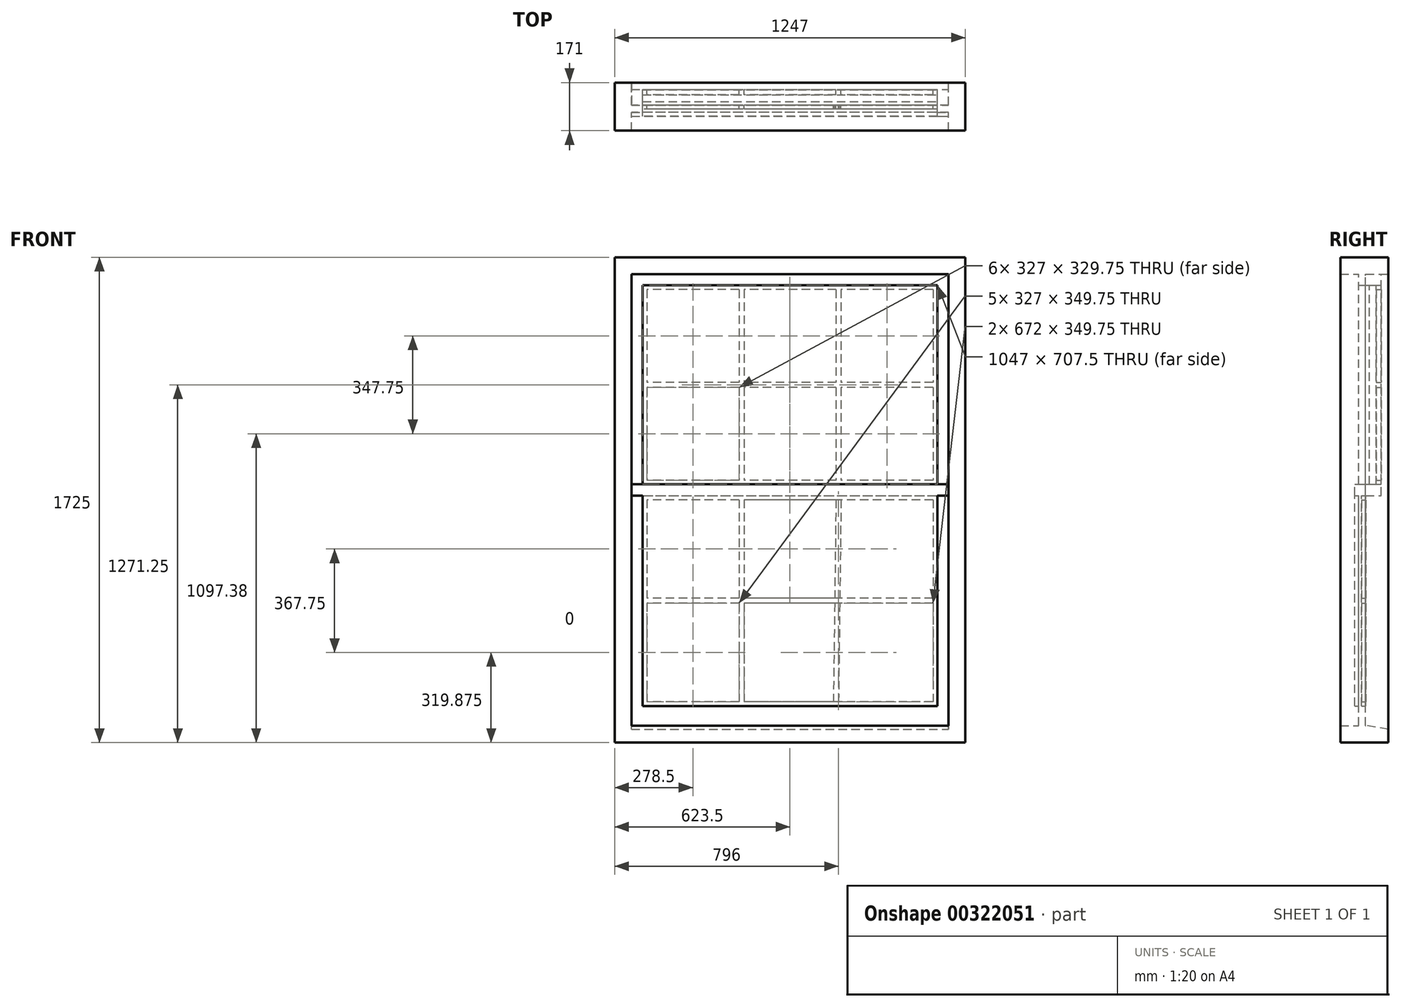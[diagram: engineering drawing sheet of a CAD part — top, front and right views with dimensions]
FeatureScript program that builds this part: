
annotation { "Feature Type Name" : "Feature", "Feature Type Description" : "" }
export const myFeature = defineFeature(function(context is Context, id is Id, definition is map)
    precondition{}
    {
        {
            var Q0;
            Q0=qCreatedBy(makeId("Front.planeOp"),FACE);
            var sketch = newSketch(context, id + "F0", { "sketchPlane" : qUnion([Q0])});
            skLineSegment(sketch, "E0.bottom", {"start": v(0, 0) * mm, "end": v(-1247, 0) * mm});
            skLineSegment(sketch, "E0.top", {"start": v(0, 1725) * mm, "end": v(-1247, 1725) * mm});
            skLineSegment(sketch, "E0.left", {"start": v(0, 0) * mm, "end": v(0, 1725) * mm});
            skLineSegment(sketch, "E0.right", {"start": v(-1247, 0) * mm, "end": v(-1247, 1725) * mm});
            skLineSegment(sketch, "E1.0", {"start": v(-60, 1665) * mm, "end": v(-1187, 1665) * mm});
            skLineSegment(sketch, "E1.1", {"start": v(-60, 60) * mm, "end": v(-60, 1665) * mm});
            skLineSegment(sketch, "E1.2", {"start": v(-60, 60) * mm, "end": v(-1187, 60) * mm});
            skLineSegment(sketch, "E1.3", {"start": v(-1187, 60) * mm, "end": v(-1187, 1665) * mm});
            skLineSegment(sketch, "E2.0", {"start": v(-1147, 130) * mm, "end": v(-1147, 877.5) * mm});
            skLineSegment(sketch, "E2.1", {"start": v(-100, 1625) * mm, "end": v(-1147, 1625) * mm});
            skLineSegment(sketch, "E2.2", {"start": v(-100, 130) * mm, "end": v(-100, 877.5) * mm});
            skLineSegment(sketch, "E3.0", {"start": v(-100, 130) * mm, "end": v(-1147, 130) * mm});
            skLineSegment(sketch, "E4", {"start": v(-1187, 877.5) * mm, "end": v(-60, 877.5) * mm});
            skLineSegment(sketch, "E5.0", {"start": v(-1147, 917.5) * mm, "end": v(-100, 917.5) * mm});
            skPoint(sketch, "E6.orphan", {"position": v(-100, 877.5) * mm});
            skPoint(sketch, "E7.orphan", {"position": v(-1147, 877.5) * mm});
            skLineSegment(sketch, "E8.trimOffspring", {"start": v(-100, 917.5) * mm, "end": v(-100, 1625) * mm});
            skLineSegment(sketch, "E9.trimOffspring", {"start": v(-1147, 917.5) * mm, "end": v(-1147, 1625) * mm});
            skLineSegment(sketch, "E10.bottom", {"start": v(-115, 1610) * mm, "end": v(-442, 1610) * mm});
            skLineSegment(sketch, "E10.top", {"start": v(-115, 1280.25) * mm, "end": v(-442, 1280.25) * mm});
            skLineSegment(sketch, "E10.left", {"start": v(-115, 1610) * mm, "end": v(-115, 1280.25) * mm});
            skLineSegment(sketch, "E10.right", {"start": v(-787, 1610) * mm, "end": v(-787, 1280.25) * mm});
            skLineSegment(sketch, "E11.bottom", {"start": v(-805, 1610) * mm, "end": v(-1132, 1610) * mm});
            skLineSegment(sketch, "E11.top", {"start": v(-805, 1280.25) * mm, "end": v(-1132, 1280.25) * mm});
            skLineSegment(sketch, "E11.left", {"start": v(-805, 1610) * mm, "end": v(-805, 1280.25) * mm});
            skLineSegment(sketch, "E11.right", {"start": v(-1132, 1610) * mm, "end": v(-1132, 1280.25) * mm});
            skLineSegment(sketch, "E12.bottom", {"start": v(-115, 1262.25) * mm, "end": v(-787, 1262.25) * mm});
            skLineSegment(sketch, "E12.top", {"start": v(-115, 932.5) * mm, "end": v(-787, 932.5) * mm});
            skLineSegment(sketch, "E12.left", {"start": v(-115, 1262.25) * mm, "end": v(-115, 932.5) * mm});
            skLineSegment(sketch, "E12.right", {"start": v(-787, 1262.25) * mm, "end": v(-787, 932.5) * mm});
            skLineSegment(sketch, "E13.bottom", {"start": v(-805, 1262.25) * mm, "end": v(-1132, 1262.25) * mm});
            skLineSegment(sketch, "E13.top", {"start": v(-805, 932.5) * mm, "end": v(-1132, 932.5) * mm});
            skLineSegment(sketch, "E13.left", {"start": v(-805, 1262.25) * mm, "end": v(-805, 932.5) * mm});
            skLineSegment(sketch, "E13.right", {"start": v(-1132, 1262.25) * mm, "end": v(-1132, 932.5) * mm});
            skLineSegment(sketch, "E14.bottom", {"start": v(-115, 862.5) * mm, "end": v(-442, 862.5) * mm});
            skLineSegment(sketch, "E14.top", {"start": v(-115, 512.75) * mm, "end": v(-446.39, 512.75) * mm});
            skLineSegment(sketch, "E14.left", {"start": v(-115, 862.5) * mm, "end": v(-115, 512.75) * mm});
            skLineSegment(sketch, "E14.right", {"start": v(-787, 862.5) * mm, "end": v(-787, 512.75) * mm});
            skLineSegment(sketch, "E15.bottom", {"start": v(-805, 862.5) * mm, "end": v(-1132, 862.5) * mm});
            skLineSegment(sketch, "E15.top", {"start": v(-805, 512.75) * mm, "end": v(-1132, 512.75) * mm});
            skLineSegment(sketch, "E15.left", {"start": v(-805, 862.5) * mm, "end": v(-805, 512.75) * mm});
            skLineSegment(sketch, "E15.right", {"start": v(-1132, 862.5) * mm, "end": v(-1132, 512.75) * mm});
            skLineSegment(sketch, "E16.bottom", {"start": v(-115, 494.75) * mm, "end": v(-446.61, 494.75) * mm});
            skLineSegment(sketch, "E16.top", {"start": v(-115, 145) * mm, "end": v(-451, 145) * mm});
            skLineSegment(sketch, "E16.left", {"start": v(-115, 494.75) * mm, "end": v(-115, 145) * mm});
            skLineSegment(sketch, "E16.right", {"start": v(-787, 494.75) * mm, "end": v(-787, 145) * mm});
            skLineSegment(sketch, "E17.bottom", {"start": v(-805, 494.75) * mm, "end": v(-1132, 494.75) * mm});
            skLineSegment(sketch, "E17.top", {"start": v(-805, 145) * mm, "end": v(-1132, 145) * mm});
            skLineSegment(sketch, "E17.left", {"start": v(-805, 494.75) * mm, "end": v(-805, 145) * mm});
            skLineSegment(sketch, "E17.right", {"start": v(-1132, 494.75) * mm, "end": v(-1132, 145) * mm});
            skLineSegment(sketch, "E18", {"start": v(-442, 1610) * mm, "end": v(-442, 1280.25) * mm});
            skLineSegment(sketch, "E19", {"start": v(-460, 1610) * mm, "end": v(-460, 1280.25) * mm});
            skLineSegment(sketch, "E20.trimOffspring", {"start": v(-460, 1610) * mm, "end": v(-787, 1610) * mm});
            skLineSegment(sketch, "E21.trimOffspring", {"start": v(-460, 1280.25) * mm, "end": v(-787, 1280.25) * mm});
            skLineSegment(sketch, "E22", {"start": v(-442, 1262.25) * mm, "end": v(-442, 932.5) * mm});
            skLineSegment(sketch, "E23", {"start": v(-460, 1262.25) * mm, "end": v(-460, 932.5) * mm});
            skLineSegment(sketch, "E24", {"start": v(-442, 862.5) * mm, "end": v(-446.39, 512.75) * mm});
            skLineSegment(sketch, "E25", {"start": v(-460, 862.5) * mm, "end": v(-464.39, 512.75) * mm});
            skLineSegment(sketch, "E26.trimOffspring", {"start": v(-460, 862.5) * mm, "end": v(-787, 862.5) * mm});
            skLineSegment(sketch, "E27.trimOffspring", {"start": v(-464.39, 512.75) * mm, "end": v(-787, 512.75) * mm});
            skLineSegment(sketch, "E28.trimOffspring", {"start": v(-464.61, 494.75) * mm, "end": v(-787, 494.75) * mm});
            skLineSegment(sketch, "E29.trimOffspring", {"start": v(-469, 145) * mm, "end": v(-787, 145) * mm});
            skLineSegment(sketch, "E30.trimOffspring", {"start": v(-446.61, 494.75) * mm, "end": v(-451, 145) * mm});
            skLineSegment(sketch, "E31.trimOffspring", {"start": v(-464.61, 494.75) * mm, "end": v(-469, 145) * mm});
            skSolve(sketch);
        }
        {
            var Q0;
            Q0=makeQuery(id+"F0.imprint","IMPRINT",FACE,{"disambiguationData":[TD([[makeQuery(id+"F0.imprint","IMPRINT",EDGE,{"derivedFrom":sQuery(id+"F0.wireOp",EDGE,"E0.bottom")}),-1.0]])]});
            extrude(context, id + "F1", {"entities" : qUnion([Q0]), "depth" : 146 * mm, "hasSecondDirection" : true, "secondDirectionOppositeDirection" : true, "secondDirectionDepth" : 25 * mm});
        }
        {
            var Q0;
            {var subQ1=sQuery(id+"F0.wireOp",EDGE,"E1.0");Q0=makeQuery(id+"F0.imprint","IMPRINT",FACE,{"disambiguationData":[TD([[makeQuery(id+"F0.imprint","IMPRINT",EDGE,{"derivedFrom":subQ1}),1.0]])]});}
            extrude(context, id + "F2", {"entities" : qUnion([Q0]), "depth" : 56 * mm});
        }
        {
            var Q0;
            {var subQ1=sQuery(id+"F0.wireOp",EDGE,"E1.2");Q0=makeQuery(id+"F0.imprint","IMPRINT",FACE,{"disambiguationData":[TD([[makeQuery(id+"F0.imprint","IMPRINT",EDGE,{"derivedFrom":subQ1}),-1.0]])]});}
            extrude(context, id + "F3", {"entities" : qUnion([Q0]), "depth" : 81 * mm, "hasSecondDirection" : true, "secondDirectionOppositeDirection" : false, "secondDirectionDepth" : 56 * mm});
        }
        {
            var Q0;
            Q0=makeQuery(id+"F0.imprint","IMPRINT",FACE,{"disambiguationData":[TD([[makeQuery(id+"F0.imprint","IMPRINT",EDGE,{"derivedFrom":sQuery(id+"F0.wireOp",EDGE,"E2.1")}),1.0]])]});
            var Q1;
            {var subQ0=sQuery(id+"F0.wireOp",EDGE,"E22");Q1=makeQuery(id+"F0.imprint","IMPRINT",FACE,{"disambiguationData":[TD([[makeQuery(id+"F0.imprint","IMPRINT",EDGE,{"derivedFrom":subQ0}),-1.0]])]});}
            extrude(context, id + "F4", {"entities" : qUnion([Q0, Q1]), "depth" : 18 * mm, "hasSecondDirection" : true, "secondDirectionOppositeDirection" : false, "secondDirectionDepth" : 1 * mm});
        }
        {
            var Q0;
            {var subQ1=sQuery(id+"F0.wireOp",EDGE,"E1.2");Q0=makeQuery(id+"F0.imprint","IMPRINT",FACE,{"disambiguationData":[TD([[makeQuery(id+"F0.imprint","IMPRINT",EDGE,{"derivedFrom":subQ1}),-1.0]])]});}
            var sketch = newSketch(context, id + "F5", { "sketchPlane" : qUnion([Q0])});
            skLineSegment(sketch, "E32.bottom", {"start": v(-115, 862.5) * mm, "end": v(-787, 862.5) * mm});
            skLineSegment(sketch, "E32.top", {"start": v(-115, 512.75) * mm, "end": v(-787, 512.75) * mm});
            skLineSegment(sketch, "E32.left", {"start": v(-115, 862.5) * mm, "end": v(-115, 512.75) * mm});
            skLineSegment(sketch, "E32.right", {"start": v(-787, 862.5) * mm, "end": v(-787, 512.75) * mm});
            skLineSegment(sketch, "E33.bottom", {"start": v(-805, 862.5) * mm, "end": v(-1132, 862.5) * mm});
            skLineSegment(sketch, "E33.top", {"start": v(-805, 512.75) * mm, "end": v(-1132, 512.75) * mm});
            skLineSegment(sketch, "E33.left", {"start": v(-805, 862.5) * mm, "end": v(-805, 512.75) * mm});
            skLineSegment(sketch, "E33.right", {"start": v(-1132, 862.5) * mm, "end": v(-1132, 512.75) * mm});
            skLineSegment(sketch, "E34.bottom", {"start": v(-115, 494.75) * mm, "end": v(-787, 494.75) * mm});
            skLineSegment(sketch, "E34.top", {"start": v(-115, 145) * mm, "end": v(-787, 145) * mm});
            skLineSegment(sketch, "E34.left", {"start": v(-115, 494.75) * mm, "end": v(-115, 145) * mm});
            skLineSegment(sketch, "E34.right", {"start": v(-787, 494.75) * mm, "end": v(-787, 145) * mm});
            skLineSegment(sketch, "E35.bottom", {"start": v(-805, 494.75) * mm, "end": v(-1132, 494.75) * mm});
            skLineSegment(sketch, "E35.top", {"start": v(-805, 145) * mm, "end": v(-1132, 145) * mm});
            skLineSegment(sketch, "E35.left", {"start": v(-805, 494.75) * mm, "end": v(-805, 145) * mm});
            skLineSegment(sketch, "E35.right", {"start": v(-1132, 494.75) * mm, "end": v(-1132, 145) * mm});
            skLineSegment(sketch, "E36.bottom", {"start": v(-100, 877.5) * mm, "end": v(-1147, 877.5) * mm});
            skLineSegment(sketch, "E36.top", {"start": v(-100, 130) * mm, "end": v(-1147, 130) * mm});
            skLineSegment(sketch, "E36.left", {"start": v(-100, 877.5) * mm, "end": v(-100, 130) * mm});
            skLineSegment(sketch, "E36.right", {"start": v(-1147, 877.5) * mm, "end": v(-1147, 130) * mm});
            skSolve(sketch);
        }
        {
            var Q0;
            Q0=makeQuery(id+"F5.imprint","IMPRINT",FACE,{"disambiguationData":[TD([[makeQuery(id+"F5.imprint","IMPRINT",EDGE,{"derivedFrom":sQuery(id+"F5.wireOp",EDGE,"E32.bottom")}),-1.0]])]});
            var Q1;
            {var subQ1=sQuery(id+"F0.wireOp",EDGE,"E2.0");Q1=makeQuery(id+"F0.imprint","IMPRINT",FACE,{"disambiguationData":[TD([[makeQuery(id+"F0.imprint","IMPRINT",EDGE,{"derivedFrom":subQ1}),-1.0]])]});}
            extrude(context, id + "F6", {"entities" : qUnion([Q0, Q1]), "depth" : 70 * mm, "hasSecondDirection" : true, "secondDirectionOppositeDirection" : false, "secondDirectionDepth" : 55 * mm});
        }
        {
            var Q0;
            Q0=makeQuery(id+"F1.opExtrude","CAP_EDGE",EDGE,{"disambiguationData":[OSD([sQuery(id+"F0.wireOp",EDGE,"E1.2")])],"isStart":true});
            chamfer(context, id + "F7", {"entities" : qUnion([Q0]), "chamferType" : ChamferType.OFFSET_ANGLE, "width" : 80 * mm, "oppositeDirection" : false, "angle" : 9 * degree, "tangentPropagation" : true});
        }
        {
            var Q0;
            Q0=makeQuery(id+"F6.opExtrude","CAP_FACE",FACE,{"disambiguationData":[OSD([sQuery(id+"F5.wireOp",EDGE,"E32.bottom"),sQuery(id+"F5.wireOp",EDGE,"E32.top"),sQuery(id+"F5.wireOp",EDGE,"E32.left"),sQuery(id+"F5.wireOp",EDGE,"E32.right"),sQuery(id+"F5.wireOp",EDGE,"E33.bottom"),sQuery(id+"F5.wireOp",EDGE,"E33.top"),sQuery(id+"F5.wireOp",EDGE,"E33.left"),sQuery(id+"F5.wireOp",EDGE,"E33.right"),sQuery(id+"F5.wireOp",EDGE,"E34.bottom"),sQuery(id+"F5.wireOp",EDGE,"E34.top"),sQuery(id+"F5.wireOp",EDGE,"E34.left"),sQuery(id+"F5.wireOp",EDGE,"E34.right"),sQuery(id+"F5.wireOp",EDGE,"E35.bottom"),sQuery(id+"F5.wireOp",EDGE,"E35.top"),sQuery(id+"F5.wireOp",EDGE,"E35.left"),sQuery(id+"F5.wireOp",EDGE,"E35.right"),sQuery(id+"F5.wireOp",EDGE,"E36.bottom"),sQuery(id+"F5.wireOp",EDGE,"E36.top"),sQuery(id+"F5.wireOp",EDGE,"E36.left"),sQuery(id+"F5.wireOp",EDGE,"E36.right")])],"isStart":false});
            var sketch = newSketch(context, id + "F8", { "sketchPlane" : qUnion([Q0])});
            skLineSegment(sketch, "E37.bottom", {"start": v(-1147, 877.5) * mm, "end": v(-100, 877.5) * mm});
            skLineSegment(sketch, "E37.top", {"start": v(-1147, 130) * mm, "end": v(-100, 130) * mm});
            skLineSegment(sketch, "E37.left", {"start": v(-1147, 877.5) * mm, "end": v(-1147, 130) * mm});
            skLineSegment(sketch, "E37.right", {"start": v(-100, 877.5) * mm, "end": v(-100, 130) * mm});
            skSolve(sketch);
        }
        {
            var Q0;
            Q0=makeQuery(id+"F8.imprint","IMPRINT",FACE,{"disambiguationData":[TD([[makeQuery(id+"F8.imprint","IMPRINT",EDGE,{"derivedFrom":sQuery(id+"F8.wireOp",EDGE,"E37.bottom")}),1.0]])]});
            var Q1;
            Q1=makeQuery(id+"F8.imprint","IMPRINT",FACE,{"disambiguationData":[TD([[makeQuery(id+"F8.imprint","IMPRINT",EDGE,{"derivedFrom":makeQuery(id+"F6.opExtrude","CAP_EDGE",EDGE,{"disambiguationData":[OSD([sQuery(id+"F5.wireOp",EDGE,"E33.bottom")])],"isStart":false})}),1.0]])]});
            var Q2;
            Q2=makeQuery(id+"F8.imprint","IMPRINT",FACE,{"disambiguationData":[TD([[makeQuery(id+"F8.imprint","IMPRINT",EDGE,{"derivedFrom":makeQuery(id+"F6.opExtrude","CAP_EDGE",EDGE,{"disambiguationData":[OSD([sQuery(id+"F5.wireOp",EDGE,"E32.bottom")])],"isStart":false})}),1.0]])]});
            var Q3;
            Q3=makeQuery(id+"F8.imprint","IMPRINT",FACE,{"disambiguationData":[TD([[makeQuery(id+"F8.imprint","IMPRINT",EDGE,{"derivedFrom":makeQuery(id+"F6.opExtrude","CAP_EDGE",EDGE,{"disambiguationData":[OSD([sQuery(id+"F5.wireOp",EDGE,"E35.bottom")])],"isStart":false})}),1.0]])]});
            var Q4;
            Q4=makeQuery(id+"F8.imprint","IMPRINT",FACE,{"disambiguationData":[TD([[makeQuery(id+"F8.imprint","IMPRINT",EDGE,{"derivedFrom":makeQuery(id+"F6.opExtrude","CAP_EDGE",EDGE,{"disambiguationData":[OSD([sQuery(id+"F5.wireOp",EDGE,"E34.bottom")])],"isStart":false})}),1.0]])]});
            extrude(context, id + "F9", {"entities" : qUnion([Q0, Q1, Q2, Q3, Q4]), "depth" : 25 * mm});
        }
        {
            var Q0;
            Q0=makeQuery(id+"F2.opExtrude","CAP_FACE",FACE,{"disambiguationData":[OSD([sQuery(id+"F0.wireOp",EDGE,"E1.0"),sQuery(id+"F0.wireOp",EDGE,"E1.1"),sQuery(id+"F0.wireOp",EDGE,"E1.3"),sQuery(id+"F0.wireOp",EDGE,"E2.1"),sQuery(id+"F0.wireOp",EDGE,"E4"),sQuery(id+"F0.wireOp",EDGE,"E5.0"),sQuery(id+"F0.wireOp",EDGE,"E8.trimOffspring"),sQuery(id+"F0.wireOp",EDGE,"E9.trimOffspring")])],"isStart":false});
            extrude(context, id + "F10", {"entities" : qUnion([Q0]), "depth" : 25 * mm});
        }
        {
            var Q0;
            Q0=makeQuery(id+"F10.opExtrude","CAP_FACE",FACE,{"disambiguationData":[OSD([sQuery(id+"F0.wireOp",EDGE,"E1.0"),sQuery(id+"F0.wireOp",EDGE,"E1.1"),sQuery(id+"F0.wireOp",EDGE,"E1.3"),sQuery(id+"F0.wireOp",EDGE,"E2.1"),sQuery(id+"F0.wireOp",EDGE,"E4"),sQuery(id+"F0.wireOp",EDGE,"E5.0"),sQuery(id+"F0.wireOp",EDGE,"E8.trimOffspring"),sQuery(id+"F0.wireOp",EDGE,"E9.trimOffspring")])],"isStart":false});
            var sketch = newSketch(context, id + "F11", { "sketchPlane" : qUnion([Q0])});
            skLineSegment(sketch, "E38", {"start": v(-1147, 917.5) * mm, "end": v(-1187, 917.5) * mm});
            skLineSegment(sketch, "E39", {"start": v(-100, 917.5) * mm, "end": v(-60, 917.5) * mm});
            skSolve(sketch);
        }
        {
            var Q0;
            {var subQ2=sQuery(id+"F11.wireOp",EDGE,"E38");Q0=makeQuery(id+"F11.imprint","IMPRINT",FACE,{"disambiguationData":[TD([[makeQuery(id+"F11.imprint","IMPRINT",EDGE,{"derivedFrom":subQ2}),1.0]])]});}
            var Q1;
            Q1=makeQuery(id+"F9.opExtrude","CAP_FACE",FACE,{"disambiguationData":[OSD([sQuery(id+"F8.wireOp",EDGE,"E37.bottom"),sQuery(id+"F8.wireOp",EDGE,"E37.top"),sQuery(id+"F8.wireOp",EDGE,"E37.left"),sQuery(id+"F8.wireOp",EDGE,"E37.right")])],"isStart":false});
            extrude(context, id + "F12", {"entities" : qUnion([Q0]), "operationType" : NewBodyOperationType.ADD, "endBound" : BoundingType.UP_TO_SURFACE, "endBoundEntityFace" : qUnion([Q1]), "depth" : 25 * mm});
        }
        {
            var Q0;
            Q0=makeQuery(id+"F4.opExtrude","CAP_FACE",FACE,{"disambiguationData":[OSD([sQuery(id+"F0.wireOp",EDGE,"E2.1"),sQuery(id+"F0.wireOp",EDGE,"E5.0"),sQuery(id+"F0.wireOp",EDGE,"E8.trimOffspring"),sQuery(id+"F0.wireOp",EDGE,"E9.trimOffspring"),sQuery(id+"F0.wireOp",EDGE,"E10.bottom"),sQuery(id+"F0.wireOp",EDGE,"E10.top"),sQuery(id+"F0.wireOp",EDGE,"E10.left"),sQuery(id+"F0.wireOp",EDGE,"E10.right"),sQuery(id+"F0.wireOp",EDGE,"E11.bottom"),sQuery(id+"F0.wireOp",EDGE,"E11.top"),sQuery(id+"F0.wireOp",EDGE,"E11.left"),sQuery(id+"F0.wireOp",EDGE,"E11.right"),sQuery(id+"F0.wireOp",EDGE,"E12.bottom"),sQuery(id+"F0.wireOp",EDGE,"E12.top"),sQuery(id+"F0.wireOp",EDGE,"E12.left"),sQuery(id+"F0.wireOp",EDGE,"E12.right"),sQuery(id+"F0.wireOp",EDGE,"E13.bottom"),sQuery(id+"F0.wireOp",EDGE,"E13.top"),sQuery(id+"F0.wireOp",EDGE,"E13.left"),sQuery(id+"F0.wireOp",EDGE,"E13.right")])],"isStart":false});
            var sketch = newSketch(context, id + "F13", { "sketchPlane" : qUnion([Q0])});
            skLineSegment(sketch, "E40.bottom", {"start": v(-1147, 1625) * mm, "end": v(-100, 1625) * mm});
            skLineSegment(sketch, "E40.top", {"start": v(-1147, 917.5) * mm, "end": v(-100, 917.5) * mm});
            skLineSegment(sketch, "E40.left", {"start": v(-1147, 1625) * mm, "end": v(-1147, 917.5) * mm});
            skLineSegment(sketch, "E40.right", {"start": v(-100, 1625) * mm, "end": v(-100, 917.5) * mm});
            skSolve(sketch);
        }
        {
            var Q0;
            Q0=makeQuery(id+"F13.imprint","IMPRINT",FACE,{"disambiguationData":[TD([[makeQuery(id+"F13.imprint","IMPRINT",EDGE,{"derivedFrom":sQuery(id+"F13.wireOp",EDGE,"E40.bottom")}),1.0]])]});
            var Q1;
            Q1=makeQuery(id+"F13.imprint","IMPRINT",FACE,{"disambiguationData":[TD([[makeQuery(id+"F13.imprint","IMPRINT",EDGE,{"derivedFrom":makeQuery(id+"F4.opExtrude","CAP_EDGE",EDGE,{"disambiguationData":[OSD([sQuery(id+"F0.wireOp",EDGE,"E12.bottom")])],"isStart":false})}),1.0]])]});
            var Q2;
            Q2=makeQuery(id+"F13.imprint","IMPRINT",FACE,{"disambiguationData":[TD([[makeQuery(id+"F13.imprint","IMPRINT",EDGE,{"derivedFrom":makeQuery(id+"F4.opExtrude","CAP_EDGE",EDGE,{"disambiguationData":[OSD([sQuery(id+"F0.wireOp",EDGE,"E13.bottom")])],"isStart":false})}),1.0]])]});
            var Q3;
            Q3=makeQuery(id+"F13.imprint","IMPRINT",FACE,{"disambiguationData":[TD([[makeQuery(id+"F13.imprint","IMPRINT",EDGE,{"derivedFrom":makeQuery(id+"F4.opExtrude","CAP_EDGE",EDGE,{"disambiguationData":[OSD([sQuery(id+"F0.wireOp",EDGE,"E11.bottom")])],"isStart":false})}),1.0]])]});
            var Q4;
            Q4=makeQuery(id+"F13.imprint","IMPRINT",FACE,{"disambiguationData":[TD([[makeQuery(id+"F13.imprint","IMPRINT",EDGE,{"derivedFrom":makeQuery(id+"F4.opExtrude","CAP_EDGE",EDGE,{"disambiguationData":[OSD([sQuery(id+"F0.wireOp",EDGE,"E10.bottom")])],"isStart":false})}),1.0]])]});
            var Q5;
            Q5=makeQuery(id+"F13.imprint","IMPRINT",FACE,{"disambiguationData":[TD([[makeQuery(id+"F13.imprint","IMPRINT",EDGE,{"derivedFrom":makeQuery(id+"F4.opExtrude","CAP_EDGE",EDGE,{"disambiguationData":[OSD([sQuery(id+"F0.wireOp",EDGE,"E10.right")])],"isStart":false})}),1.0]])]});
            extrude(context, id + "F14", {"entities" : qUnion([Q0, Q1, Q2, Q3, Q4, Q5]), "depth" : 25 * mm});
        }
    });
